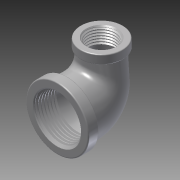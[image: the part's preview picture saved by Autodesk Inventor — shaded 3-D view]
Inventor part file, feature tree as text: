
AUTODESK INVENTOR PART (.ipt)
format: ipt  version: 2013 SP2 (Build 170200200, 200)  size: 1,785,856 bytes
history: native  units: in
note: dims shown in document units (in); Inventor stores cm internally (conversion verified against a paired STEP export)
features: other x2, sketch x2, imported_body x1
ambient origin geometry x8: Origin, YZ Plane, XZ Plane, XY Plane, X Axis, Y Axis, Z Axis, Center Point
feature tree (5):
  parser-record x1  (decoder bookkeeping rows leaked as tree rows — omitted from the tree; the rows remain in map.json)
  other  "44605K4221"
  sketch  "Sketch1"  dims[d0=0.43in]
  sketch  "Sketch2"  dims[d1=0.58in]
  imported_body  "Base1"
